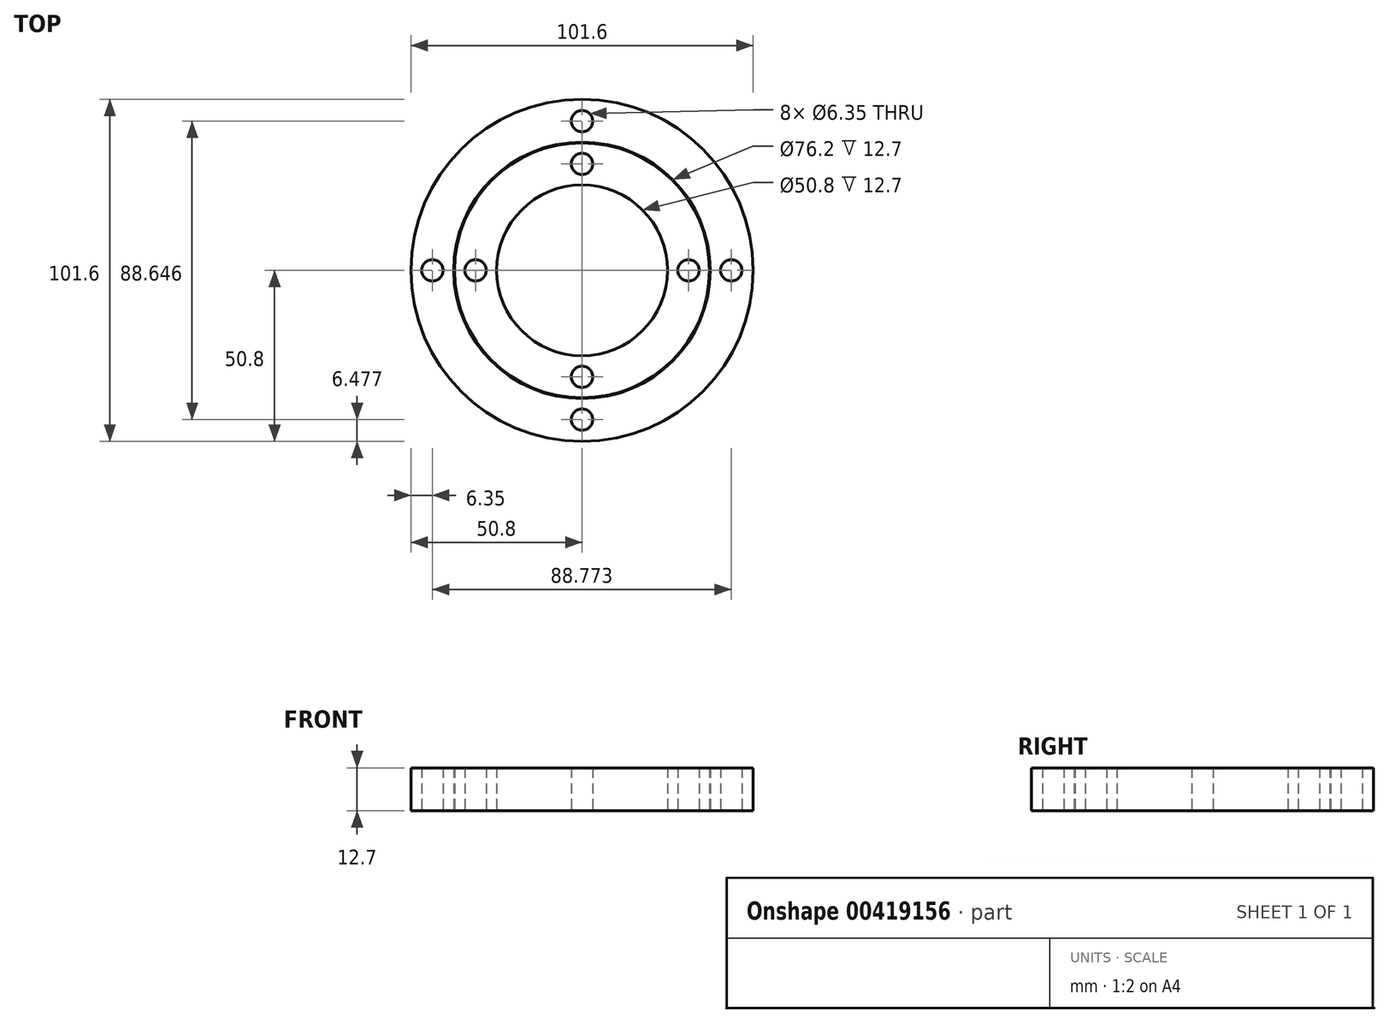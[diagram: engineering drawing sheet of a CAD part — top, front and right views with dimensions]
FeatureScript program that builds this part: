
annotation { "Feature Type Name" : "Feature", "Feature Type Description" : "" }
export const myFeature = defineFeature(function(context is Context, id is Id, definition is map)
    precondition{}
    {
        {
            var Q0;
            Q0=qCreatedBy(makeId("Top.planeOp"),FACE);
            var sketch = newSketch(context, id + "F0", { "sketchPlane" : qUnion([Q0])});
            skCircle(sketch, "E0", {"center": v(0, 0) * mm, "radius": 50.8 * mm});
            skCircle(sketch, "E1", {"center": v(0, 0) * mm, "radius": 38.1 * mm});
            skCircle(sketch, "E2", {"center": v(0, 0) * mm, "radius": 25.4 * mm});
            skCircle(sketch, "E3", {"center": v(0, 0) * mm, "radius": 37.85 * mm});
            skLineSegment(sketch, "E4", {"start": v(-50.8, 0) * mm, "end": v(-38.1, 0) * mm});
            skLineSegment(sketch, "E5", {"start": v(0, 50.8) * mm, "end": v(0, 37.85) * mm});
            skLineSegment(sketch, "E6", {"start": v(37.85, 0) * mm, "end": v(50.8, 0) * mm});
            skLineSegment(sketch, "E7", {"start": v(0, 25.4) * mm, "end": v(0, 37.85) * mm});
            skLineSegment(sketch, "E8", {"start": v(-25.4, 0) * mm, "end": v(-37.85, 0) * mm});
            skLineSegment(sketch, "E9", {"start": v(0, -25.4) * mm, "end": v(0, -37.85) * mm});
            skLineSegment(sketch, "E10", {"start": v(25.4, 0) * mm, "end": v(37.85, 0) * mm});
            skLineSegment(sketch, "E11", {"start": v(0, -37.85) * mm, "end": v(0, -50.8) * mm});
            skCircle(sketch, "E12", {"center": v(-44.45, 0) * mm, "radius": 3.18 * mm});
            skCircle(sketch, "E13", {"center": v(-31.62, 0) * mm, "radius": 3.18 * mm});
            skCircle(sketch, "E14", {"center": v(0, -44.32) * mm, "radius": 3.18 * mm});
            skCircle(sketch, "E15", {"center": v(0, 44.32) * mm, "radius": 3.18 * mm});
            skCircle(sketch, "E16", {"center": v(0, 31.62) * mm, "radius": 3.18 * mm});
            skCircle(sketch, "E17", {"center": v(44.32, 0) * mm, "radius": 3.18 * mm});
            skCircle(sketch, "E18", {"center": v(0, -31.62) * mm, "radius": 3.18 * mm});
            skCircle(sketch, "E19", {"center": v(31.62, 0) * mm, "radius": 3.18 * mm});
            skSolve(sketch);
        }
        {
            var Q0;
            {var subQ0=sQuery(id+"F0.wireOp",EDGE,"E7");var subQ5=sQuery(id+"F0.wireOp",EDGE,"E2");var subQ6=makeQuery(id+"F0.imprint","INTERSECT",VERTEX,{"derivedFrom":[subQ5,subQ0]});Q0=makeQuery(id+"F0.imprint","IMPRINT",FACE,{"disambiguationData":[TD([[makeQuery(id+"F0.imprint","IMPRINT",EDGE,{"disambiguationData":[TD([[subQ6,1.0]])],"derivedFrom":subQ5}),-1.0]])]});}
            var Q1;
            {var subQ0=sQuery(id+"F0.wireOp",EDGE,"E5");var subQ5=sQuery(id+"F0.wireOp",EDGE,"E0");var subQ6=makeQuery(id+"F0.imprint","INTERSECT",VERTEX,{"derivedFrom":[subQ5,subQ0]});Q1=makeQuery(id+"F0.imprint","IMPRINT",FACE,{"disambiguationData":[TD([[makeQuery(id+"F0.imprint","IMPRINT",EDGE,{"disambiguationData":[TD([[subQ6,1.0]])],"derivedFrom":subQ5}),1.0]])]});}
            var Q2;
            {var subQ0=sQuery(id+"F0.wireOp",EDGE,"E7");var subQ1=sQuery(id+"F0.wireOp",EDGE,"E2");var subQ2=makeQuery(id+"F0.imprint","INTERSECT",VERTEX,{"derivedFrom":[subQ1,subQ0]});Q2=makeQuery(id+"F0.imprint","IMPRINT",FACE,{"disambiguationData":[TD([[makeQuery(id+"F0.imprint","IMPRINT",EDGE,{"disambiguationData":[TD([[subQ2,-1.0]])],"derivedFrom":subQ1}),-1.0]])]});}
            var Q3;
            {var subQ0=sQuery(id+"F0.wireOp",EDGE,"E4");var subQ7=sQuery(id+"F0.wireOp",EDGE,"E0");var subQ8=makeQuery(id+"F0.imprint","INTERSECT",VERTEX,{"derivedFrom":[subQ7,subQ0]});Q3=makeQuery(id+"F0.imprint","IMPRINT",FACE,{"disambiguationData":[TD([[makeQuery(id+"F0.imprint","IMPRINT",EDGE,{"disambiguationData":[TD([[subQ8,1.0]])],"derivedFrom":subQ7}),1.0]])]});}
            var Q4;
            {var subQ0=sQuery(id+"F0.wireOp",EDGE,"E4");var subQ9=sQuery(id+"F0.wireOp",EDGE,"E0");var subQ10=makeQuery(id+"F0.imprint","INTERSECT",VERTEX,{"derivedFrom":[subQ9,subQ0]});Q4=makeQuery(id+"F0.imprint","IMPRINT",FACE,{"disambiguationData":[TD([[makeQuery(id+"F0.imprint","IMPRINT",EDGE,{"disambiguationData":[TD([[subQ10,-1.0]])],"derivedFrom":subQ9}),1.0]])]});}
            var Q5;
            {var subQ0=sQuery(id+"F0.wireOp",EDGE,"E9");var subQ1=sQuery(id+"F0.wireOp",EDGE,"E2");var subQ2=makeQuery(id+"F0.imprint","INTERSECT",VERTEX,{"derivedFrom":[subQ1,subQ0]});Q5=makeQuery(id+"F0.imprint","IMPRINT",FACE,{"disambiguationData":[TD([[makeQuery(id+"F0.imprint","IMPRINT",EDGE,{"disambiguationData":[TD([[subQ2,-1.0]])],"derivedFrom":subQ1}),-1.0]])]});}
            var Q6;
            {var subQ0=sQuery(id+"F0.wireOp",EDGE,"E6");var subQ1=sQuery(id+"F0.wireOp",EDGE,"E0");var subQ2=makeQuery(id+"F0.imprint","INTERSECT",VERTEX,{"derivedFrom":[subQ1,subQ0]});Q6=makeQuery(id+"F0.imprint","IMPRINT",FACE,{"disambiguationData":[TD([[makeQuery(id+"F0.imprint","IMPRINT",EDGE,{"disambiguationData":[TD([[subQ2,1.0]])],"derivedFrom":subQ1}),1.0]])]});}
            var Q7;
            {var subQ0=sQuery(id+"F0.wireOp",EDGE,"E8");var subQ5=sQuery(id+"F0.wireOp",EDGE,"E2");var subQ6=makeQuery(id+"F0.imprint","INTERSECT",VERTEX,{"derivedFrom":[subQ5,subQ0]});Q7=makeQuery(id+"F0.imprint","IMPRINT",FACE,{"disambiguationData":[TD([[makeQuery(id+"F0.imprint","IMPRINT",EDGE,{"disambiguationData":[TD([[subQ6,-1.0]])],"derivedFrom":subQ5}),-1.0]])]});}
            extrude(context, id + "F1", {"entities" : qUnion([Q0, Q1, Q2, Q3, Q4, Q5, Q6, Q7]), "depth" : 12.7 * mm});
        }
    });
